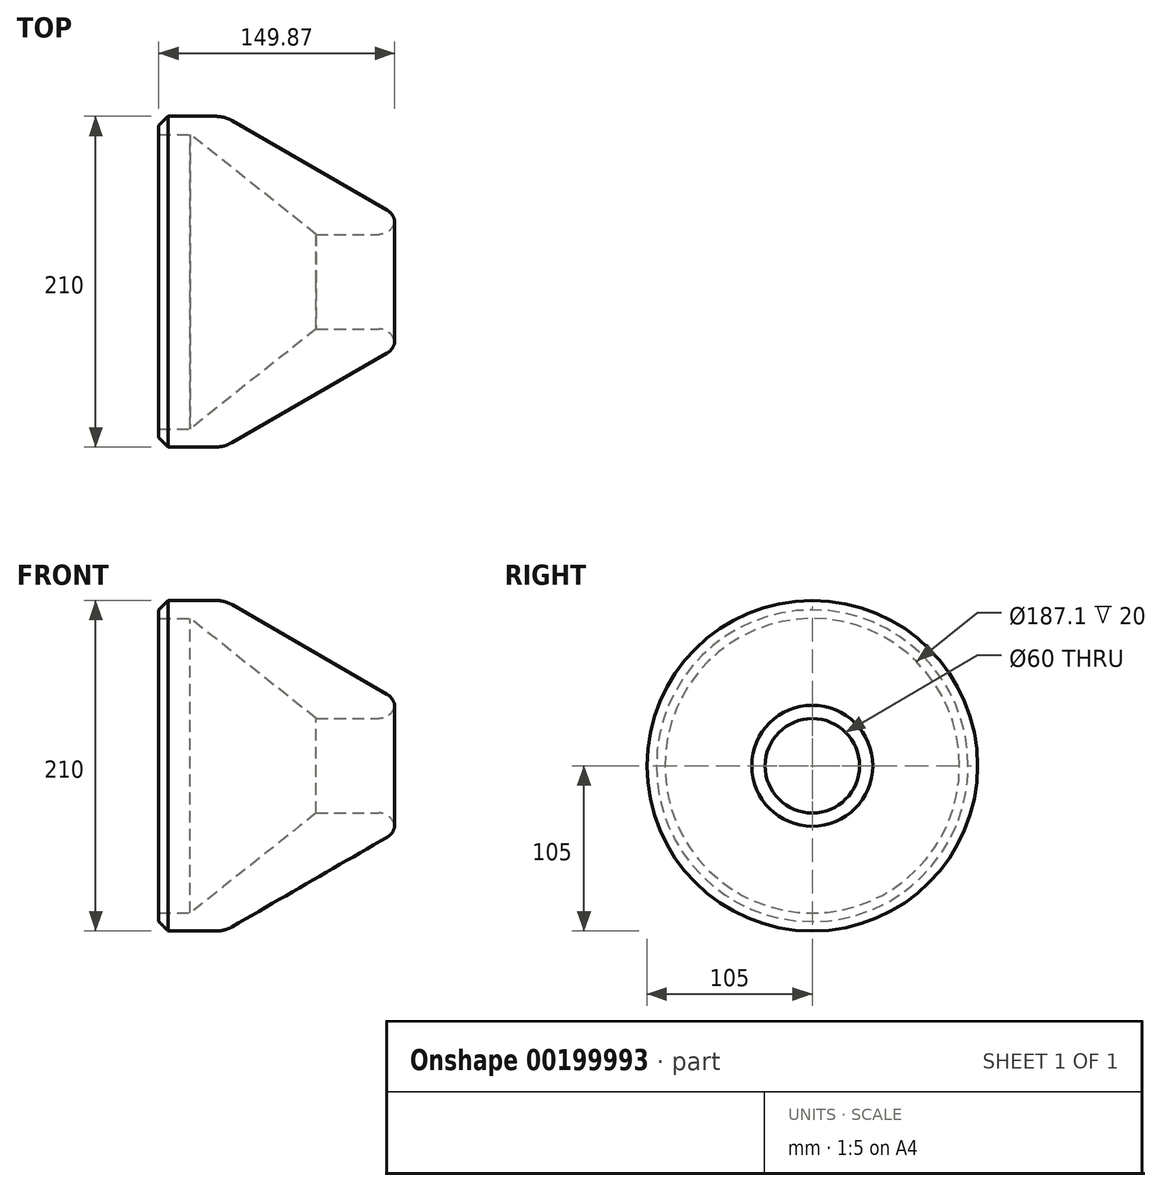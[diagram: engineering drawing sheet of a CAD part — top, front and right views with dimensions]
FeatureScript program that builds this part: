
annotation { "Feature Type Name" : "Feature", "Feature Type Description" : "" }
export const myFeature = defineFeature(function(context is Context, id is Id, definition is map)
    precondition{}
    {
        {
            var Q0;
            Q0=qCreatedBy(makeId("Front.planeOp"),FACE);
            var sketch = newSketch(context, id + "F0", { "sketchPlane" : qUnion([Q0])});
            skLineSegment(sketch, "E0", {"start": v(-113.6, 105) * mm, "end": v(-150, 105) * mm});
            skLineSegment(sketch, "E1.0", {"start": v(-150, 93.55) * mm, "end": v(-150, 105) * mm});
            skLineSegment(sketch, "E2.0", {"start": v(-93.4, 85) * mm, "end": v(-93.6, 85) * mm});
            skArc(sketch, "E3", {"start": v(-103.6, 102.32) * mm, "mid": v(-108.42, 104.32) * mm, "end": v(-113.6, 105) * mm});
            skLineSegment(sketch, "E4", {"start": v(-103.6, 102.32) * mm, "end": v(-5, 45.4) * mm});
            skLineSegment(sketch, "E5", {"start": v(-50, 30) * mm, "end": v(-10, 30) * mm});
            skLineSegment(sketch, "E6", {"start": v(0, 0) * mm, "end": v(-150, 0) * mm});
            skArc(sketch, "E7", {"start": v(-10, 30) * mm, "mid": v(-3.53, 32.37) * mm, "end": v(-0.13, 38.37) * mm});
            skArc(sketch, "E8.trimOffspring", {"start": v(-0.13, 38.37) * mm, "mid": v(-1.78, 42.43) * mm, "end": v(-5, 45.4) * mm});
            skLineSegment(sketch, "E9", {"start": v(-150, 93.55) * mm, "end": v(-130, 93.55) * mm});
            skLineSegment(sketch, "E10", {"start": v(-50, 30) * mm, "end": v(-130, 93.55) * mm});
            skSolve(sketch);
        }
        {
            var Q0;
            Q0 = qSketchRegion(id + "F0", true);
            var Q1;
            Q1=sQuery(id+"F0.wireOp",EDGE,"E6");
            revolve(context, id + "F1", {"entities" : qUnion([Q0]), "axis" : qUnion([Q1]), "revolveType" : RevolveType.FULL});
        }
        {
            var Q0;
            Q0=makeQuery(id+"F1.opRevolve","SWEPT_EDGE",EDGE,{"disambiguationData":[OSD([sQuery(id+"F0.wireOp",EDGE,"E0"),sQuery(id+"F0.wireOp",EDGE,"E1.0")])]});
            chamfer(context, id + "F2", {"entities" : qUnion([Q0]), "width" : 6 * mm, "tangentPropagation" : true});
        }
    });
